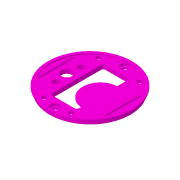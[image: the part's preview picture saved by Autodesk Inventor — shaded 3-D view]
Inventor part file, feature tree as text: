
AUTODESK INVENTOR PART (.ipt)
format: ipt  version: 2018 (Build 220112000, 112)  size: 297,472 bytes
history: native  units: mm
features: sketch x13, extrude x12, fillet x3, plane x2, revolve x1, mirror x1, chamfer x1, pattern_circular x1
ambient origin geometry x8: Origin, YZ Plane, XZ Plane, XY Plane, X Axis, Y Axis, Z Axis, Center Point
bodies: Solid1 (feature_tree)
feature tree (34):
  plane  "Work Plane5"
  sketch  "Sketch6"  dims[d32=25.4mm d33=4.0mm d34=0.0mm]
  extrude  "Extrusion6"  Depth=4.0mm TaperAngle=0.0deg
  revolve  "Revolution1"  [1 undecoded]
  plane  "Work Plane3"
  extrude  "Extrusion7"  Depth=1.0mm
  extrude  "Extrusion10"  Depth=30.48mm
  mirror  "Mirror1"
  chamfer  "Chamfer2"  Distance=4.0mm
  extrude  "Extrusion11"  Depth=33.02mm
  pattern_circular  "Circular Pattern4"  [2 undecoded]
  extrude  "Extrusion12"  Depth=0.5mm TaperAngle=360.0deg
  extrude  "Extrusion13"  Depth=0.5mm
  extrude  "Extrusion14"  Depth=0.5mm TaperAngle=0.0deg
  extrude  "Extrusion15"  Depth=0.5mm
  fillet  "Fillet5"  Radius=2.2mm
  extrude  "Extrusion16"  Depth=0.5mm
  extrude  "Extrusion17"  Depth=0.5mm
  extrude  "Extrusion18"  Depth=0.5mm
  extrude  "Extrusion19"  Depth=10.0mm TaperAngle=0.0deg
  fillet  "Fillet7"  [1 undecoded]
  fillet  "Fillet8"  [1 undecoded]
  sketch  "Sketch7"  dims[d35=90.0deg d41=63.5mm d42=69.85mm]
  sketch  "Sketch10"  dims[d43=1.0mm d44=1.0mm]
  sketch  "Sketch13"  dims[d45=1.5875mm d46=30.48mm]
  sketch  "Sketch14"  dims[d47=12.7mm]
  sketch  "Sketch15"  dims[d48=4.4mm d49=4.0mm d50=0.0mm]
  sketch  "Sketch16"  dims[d58=1.778mm d59=33.02mm]
  sketch  "Sketch18"  dims[d60=16.51mm]
  sketch  "Sketch20"  dims[d61=30.48mm]
  sketch  "Sketch21"  dims[d62=3.0mm d63=0.0mm]
  sketch  "Sketch22"  dims[d67=0.5mm d68=2.0mm d69=45.0deg]
  sketch  "Sketch23"  dims[d70=4.85mm]
  sketch  "Sketch24"  dims[d71=33.02mm d72=25.75mm d73=0.0mm d74=20.0mm d75=360.0deg d77=8.0mm d78=3.0mm d79=0.0mm d80=7.5mm d81=2.2mm d82=0.0mm d83=4.4mm d84=27.6098mm d85=19.558mm d86=10.0mm d87=0.0mm d89=30.0deg d90=30.0deg d94=50.0mm d95=25.0mm d96=25.0mm d97=12.5mm d98=10.0mm d99=0.0mm d100=2.0mm d102=8.0mm d103=8.0mm d104=3.0mm d105=0.0mm d106=10.0mm d107=22.0mm d108=5.0mm d109=0.0mm d110=5.5mm d111=20.0mm d112=12.0mm d114=33.429993mm d115=0.5mm d116=0.0mm d117=24.0mm d118=2.0mm d119=0.0mm d121=0.0mm d122=9.736mm d123=2.0mm d124=2.0mm d126=0.5mm d127=0.0mm]
note: 5 required parameter values undecoded (feature->parameter linkage not recoverable at this tier; creation-order binding heuristic only, values carry confidence <= 0.55)